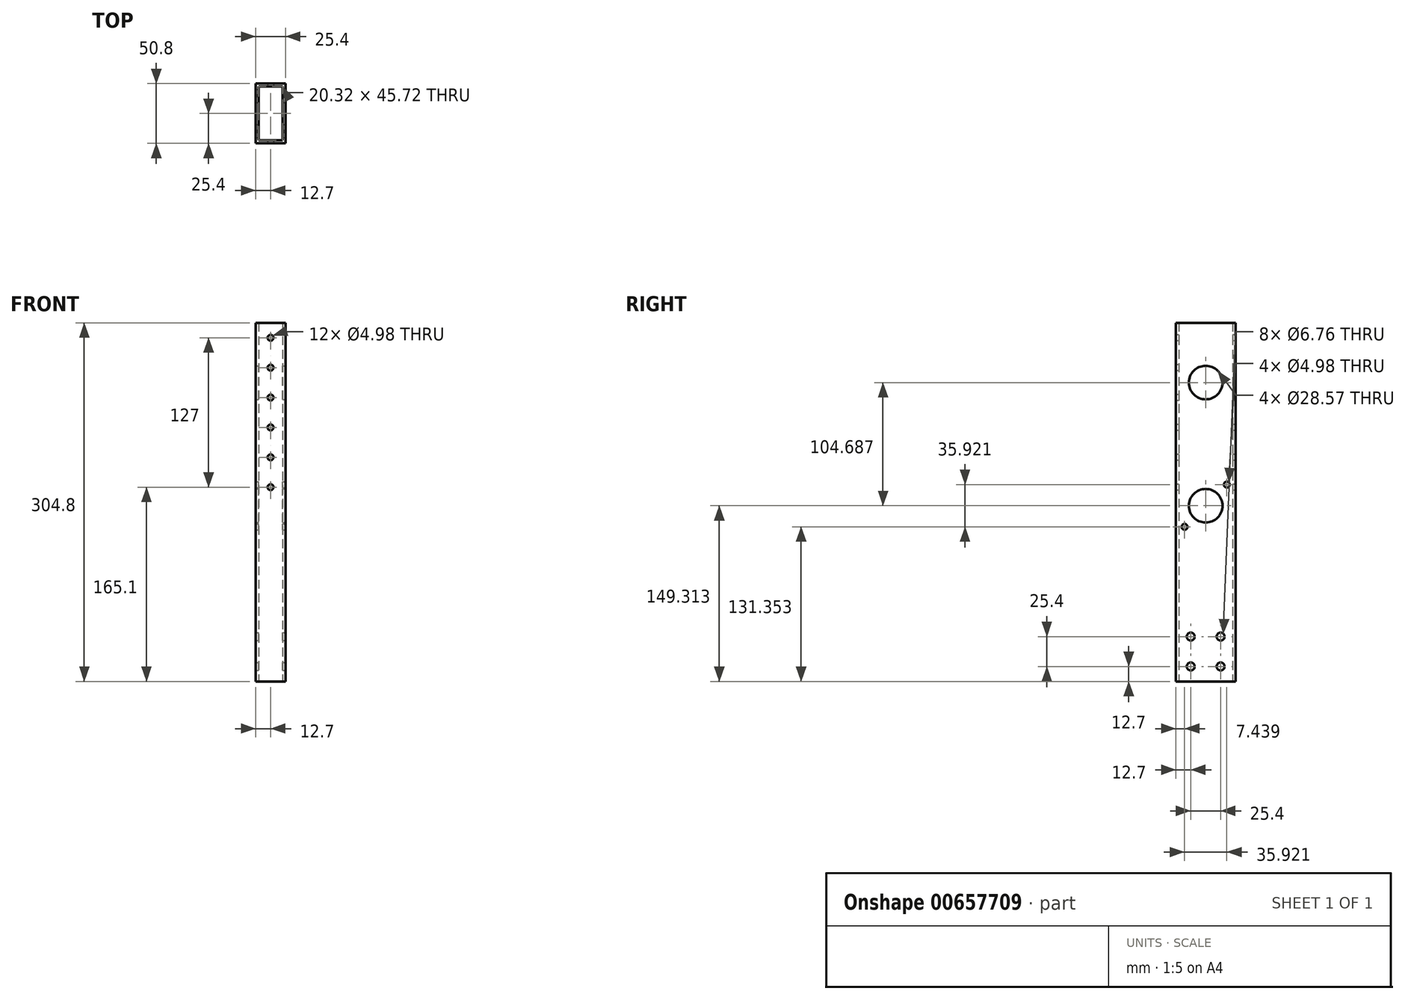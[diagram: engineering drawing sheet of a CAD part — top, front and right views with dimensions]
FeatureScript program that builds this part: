
annotation { "Feature Type Name" : "Feature", "Feature Type Description" : "" }
export const myFeature = defineFeature(function(context is Context, id is Id, definition is map)
    precondition{}
    {
        {
            var Q0;
            Q0=qCreatedBy(makeId("Top.planeOp"),FACE);
            var sketch = newSketch(context, id + "F0", { "sketchPlane" : qUnion([Q0])});
            skLineSegment(sketch, "E0.bottom", {"start": v(0, 0) * mm, "end": v(25.4, 0) * mm});
            skLineSegment(sketch, "E0.top", {"start": v(0, -50.8) * mm, "end": v(25.4, -50.8) * mm});
            skLineSegment(sketch, "E0.left", {"start": v(0, 0) * mm, "end": v(0, -50.8) * mm});
            skLineSegment(sketch, "E0.right", {"start": v(25.4, 0) * mm, "end": v(25.4, -50.8) * mm});
            skLineSegment(sketch, "E1.bottom", {"start": v(2.54, -2.54) * mm, "end": v(22.86, -2.54) * mm});
            skLineSegment(sketch, "E1.top", {"start": v(2.54, -48.26) * mm, "end": v(22.86, -48.26) * mm});
            skLineSegment(sketch, "E1.left", {"start": v(2.54, -2.54) * mm, "end": v(2.54, -48.26) * mm});
            skLineSegment(sketch, "E1.right", {"start": v(22.86, -2.54) * mm, "end": v(22.86, -48.26) * mm});
            skSolve(sketch);
        }
        {
            var Q0;
            Q0=makeQuery(id+"F0.imprint","IMPRINT",FACE,{"disambiguationData":[TD([[makeQuery(id+"F0.imprint","IMPRINT",EDGE,{"derivedFrom":sQuery(id+"F0.wireOp",EDGE,"E0.bottom")}),-1.0]])]});
            extrude(context, id + "F1", {"entities" : qUnion([Q0]), "depth" : 304.8 * mm, "offsetDistance" : 25.4 * mm});
        }
        {
            var Q0;
            Q0=makeQuery(id+"F1.opExtrude","SWEPT_FACE",FACE,{"disambiguationData":[OSD([sQuery(id+"F0.wireOp",EDGE,"E0.right")])]});
            var sketch = newSketch(context, id + "F2", { "sketchPlane" : qUnion([Q0])});
            skCircle(sketch, "E2", {"center": v(-25.4, 254) * mm, "radius": 14.29 * mm});
            skCircle(sketch, "E3", {"center": v(-38.1, 12.7) * mm, "radius": 3.38 * mm});
            skCircle(sketch, "E4.0.1.0", {"center": v(-38.1, 38.1) * mm, "radius": 3.38 * mm});
            skCircle(sketch, "E4.1.0.0", {"center": v(-12.7, 12.7) * mm, "radius": 3.38 * mm});
            skCircle(sketch, "E4.1.1.0", {"center": v(-12.7, 38.1) * mm, "radius": 3.38 * mm});
            skLineSegment(sketch, "E4.direction1", {"start": v(-38.1, 12.7) * mm, "end": v(-12.7, 12.7) * mm, "construction": true});
            skLineSegment(sketch, "E4.direction2", {"start": v(-38.1, 12.7) * mm, "end": v(-38.1, 38.1) * mm, "construction": true});
            skCircle(sketch, "E5", {"center": v(-25.4, 149.31) * mm, "radius": 14.29 * mm});
            skCircle(sketch, "E6", {"center": v(-25.4, 149.31) * mm, "radius": 25.4 * mm, "construction": true});
            skCircle(sketch, "E7", {"center": v(-7.44, 167.27) * mm, "radius": 2.49 * mm});
            skLineSegment(sketch, "E8", {"start": v(-25.4, 149.31) * mm, "end": v(-7.44, 167.27) * mm});
            skLineSegment(sketch, "E9", {"start": v(-25.4, 149.31) * mm, "end": v(0, 149.31) * mm});
            skCircle(sketch, "E10.1.0", {"center": v(-43.36, 131.35) * mm, "radius": 2.49 * mm});
            skSolve(sketch);
        }
        {
            var Q0;
            Q0=makeQuery(id+"F2.imprint","IMPRINT",FACE,{"disambiguationData":[TD([[makeQuery(id+"F2.imprint","IMPRINT",EDGE,{"derivedFrom":sQuery(id+"F2.wireOp",EDGE,"E2")}),1.0]])]});
            var Q1;
            Q1=makeQuery(id+"F2.imprint","IMPRINT",FACE,{"disambiguationData":[TD([[makeQuery(id+"F2.imprint","IMPRINT",EDGE,{"derivedFrom":sQuery(id+"F2.wireOp",EDGE,"E4.0.1.0")}),1.0]])]});
            var Q2;
            Q2=makeQuery(id+"F2.imprint","IMPRINT",FACE,{"disambiguationData":[TD([[makeQuery(id+"F2.imprint","IMPRINT",EDGE,{"derivedFrom":sQuery(id+"F2.wireOp",EDGE,"E3")}),1.0]])]});
            var Q3;
            Q3=makeQuery(id+"F2.imprint","IMPRINT",FACE,{"disambiguationData":[TD([[makeQuery(id+"F2.imprint","IMPRINT",EDGE,{"derivedFrom":sQuery(id+"F2.wireOp",EDGE,"E4.1.1.0")}),1.0]])]});
            var Q4;
            Q4=makeQuery(id+"F2.imprint","IMPRINT",FACE,{"disambiguationData":[TD([[makeQuery(id+"F2.imprint","IMPRINT",EDGE,{"derivedFrom":sQuery(id+"F2.wireOp",EDGE,"E4.1.0.0")}),1.0]])]});
            var Q5;
            Q5=makeQuery(id+"F2.imprint","IMPRINT",FACE,{"disambiguationData":[TD([[makeQuery(id+"F2.imprint","IMPRINT",EDGE,{"derivedFrom":sQuery(id+"F2.wireOp",EDGE,"E7")}),1.0]])]});
            var Q6;
            Q6=makeQuery(id+"F2.imprint","IMPRINT",FACE,{"disambiguationData":[TD([[makeQuery(id+"F2.imprint","IMPRINT",EDGE,{"derivedFrom":sQuery(id+"F2.wireOp",EDGE,"E10.1.0")}),1.0]])]});
            var Q7;
            {var subQ0=sQuery(id+"F2.wireOp",EDGE,"E8");var subQ1=sQuery(id+"F2.wireOp",EDGE,"E5");var subQ2=makeQuery(id+"F2.imprint","INTERSECT",VERTEX,{"derivedFrom":[subQ1,subQ0]});Q7=makeQuery(id+"F2.imprint","IMPRINT",FACE,{"disambiguationData":[TD([[makeQuery(id+"F2.imprint","IMPRINT",EDGE,{"disambiguationData":[TD([[subQ2,-1.0]])],"derivedFrom":subQ1}),1.0]])]});}
            var Q8;
            {var subQ0=sQuery(id+"F2.wireOp",EDGE,"E8");var subQ1=sQuery(id+"F2.wireOp",EDGE,"E5");var subQ2=makeQuery(id+"F2.imprint","INTERSECT",VERTEX,{"derivedFrom":[subQ1,subQ0]});Q8=makeQuery(id+"F2.imprint","IMPRINT",FACE,{"disambiguationData":[TD([[makeQuery(id+"F2.imprint","IMPRINT",EDGE,{"disambiguationData":[TD([[subQ2,1.0]])],"derivedFrom":subQ1}),1.0]])]});}
            extrude(context, id + "F3", {"entities" : qUnion([Q0, Q1, Q2, Q3, Q4, Q5, Q6, Q7, Q8]), "operationType" : NewBodyOperationType.REMOVE, "oppositeDirection" : true, "depth" : 25.4 * mm, "offsetDistance" : 25.4 * mm});
        }
        {
            var Q0;
            Q0=makeQuery(id+"F1.opExtrude","SWEPT_FACE",FACE,{"disambiguationData":[OSD([sQuery(id+"F0.wireOp",EDGE,"E0.top")])]});
            var sketch = newSketch(context, id + "F4", { "sketchPlane" : qUnion([Q0])});
            skCircle(sketch, "E11", {"center": v(12.7, 292.1) * mm, "radius": 2.49 * mm});
            skCircle(sketch, "E12.0.1.0", {"center": v(12.7, 266.7) * mm, "radius": 2.49 * mm});
            skCircle(sketch, "E12.0.2.0", {"center": v(12.7, 241.3) * mm, "radius": 2.49 * mm});
            skCircle(sketch, "E12.0.3.0", {"center": v(12.7, 215.9) * mm, "radius": 2.49 * mm});
            skCircle(sketch, "E12.0.4.0", {"center": v(12.7, 190.5) * mm, "radius": 2.49 * mm});
            skCircle(sketch, "E12.0.5.0", {"center": v(12.7, 165.1) * mm, "radius": 2.49 * mm});
            skLineSegment(sketch, "E12.direction1", {"start": v(12.7, 292.1) * mm, "end": v(38.1, 292.1) * mm, "construction": true});
            skLineSegment(sketch, "E12.direction2", {"start": v(12.7, 292.1) * mm, "end": v(12.7, 266.7) * mm, "construction": true});
            skSolve(sketch);
        }
        {
            var Q0;
            Q0 = qSketchRegion(id + "F4", true);
            extrude(context, id + "F5", {"entities" : qUnion([Q0]), "operationType" : NewBodyOperationType.REMOVE, "endBound" : BoundingType.THROUGH_ALL, "oppositeDirection" : true, "depth" : 25.4 * mm, "offsetDistance" : 25.4 * mm});
        }
    });
